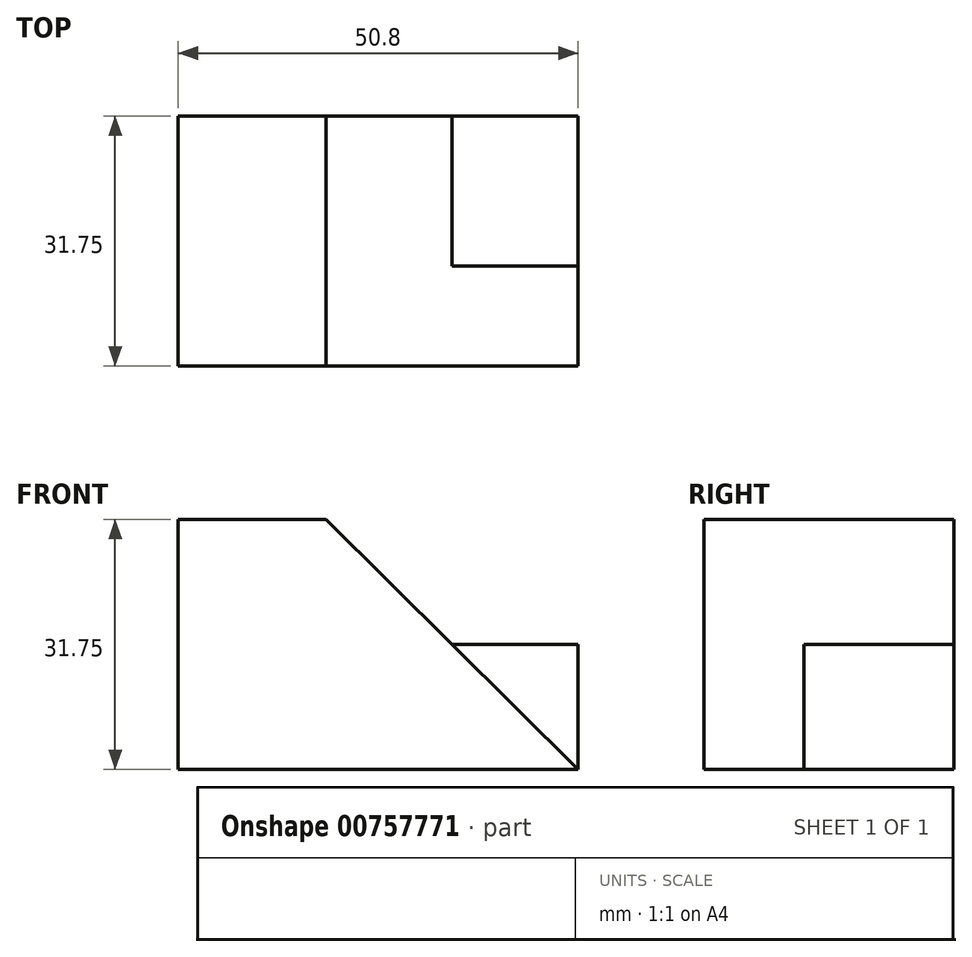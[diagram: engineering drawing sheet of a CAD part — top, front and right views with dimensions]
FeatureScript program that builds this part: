
annotation { "Feature Type Name" : "Feature", "Feature Type Description" : "" }
export const myFeature = defineFeature(function(context is Context, id is Id, definition is map)
    precondition{}
    {
        {
            var Q0;
            Q0=qCreatedBy(makeId("Front.planeOp"),FACE);
            var sketch = newSketch(context, id + "F0", { "sketchPlane" : qUnion([Q0])});
            skLineSegment(sketch, "E0", {"start": v(-18.76, 0) * mm, "end": v(32.04, 0) * mm});
            skLineSegment(sketch, "E1", {"start": v(32.04, 0) * mm, "end": v(32.04, 31.75) * mm});
            skLineSegment(sketch, "E2", {"start": v(32.04, 31.75) * mm, "end": v(-18.76, 31.75) * mm});
            skLineSegment(sketch, "E3", {"start": v(-18.76, 31.75) * mm, "end": v(-18.76, 0) * mm});
            skSolve(sketch);
        }
        {
            var Q0;
            Q0 = qSketchRegion(id + "F0", true);
            extrude(context, id + "F1", {"entities" : qUnion([Q0]), "depth" : 31.75 * mm, "offsetDistance" : 25.4 * mm});
        }
        {
            var Q0;
            Q0=makeQuery(id+"F1.opExtrude","CAP_FACE",FACE,{"disambiguationData":[OSD([sQuery(id+"F0.wireOp",EDGE,"E0"),sQuery(id+"F0.wireOp",EDGE,"E1"),sQuery(id+"F0.wireOp",EDGE,"E2"),sQuery(id+"F0.wireOp",EDGE,"E3")])],"isStart":false});
            var sketch = newSketch(context, id + "F2", { "sketchPlane" : qUnion([Q0])});
            skLineSegment(sketch, "E4", {"start": v(32.04, 0) * mm, "end": v(0, 31.75) * mm});
            skSolve(sketch);
        }
        {
            var Q0;
            {var subQ0=sQuery(id+"F2.wireOp",EDGE,"E4");Q0=makeQuery(id+"F2.imprint","IMPRINT",FACE,{"disambiguationData":[TD([[makeQuery(id+"F2.imprint","IMPRINT",EDGE,{"derivedFrom":subQ0}),-1.0]])]});}
            extrude(context, id + "F3", {"entities" : qUnion([Q0]), "operationType" : NewBodyOperationType.REMOVE, "oppositeDirection" : true, "depth" : 12.7 * mm, "offsetDistance" : 25.4 * mm});
        }
        {
            var Q0;
            Q0=makeQuery(id+"F3.boolean.opBoolean","COPY",FACE,{"derivedFrom":makeQuery(id+"F3.opExtrude","CAP_FACE",FACE,{"disambiguationData":[OSD([sQuery(id+"F0.wireOp",EDGE,"E1"),sQuery(id+"F0.wireOp",EDGE,"E2"),sQuery(id+"F2.wireOp",EDGE,"E4")])],"isStart":false})});
            var sketch = newSketch(context, id + "F4", { "sketchPlane" : qUnion([Q0])});
            skLineSegment(sketch, "E5", {"start": v(32.04, 0) * mm, "end": v(32.04, 15.88) * mm});
            skLineSegment(sketch, "E6", {"start": v(32.04, 15.88) * mm, "end": v(16.02, 15.87) * mm});
            skSolve(sketch);
        }
        {
            var Q0;
            Q0 = qSketchRegion(id + "F4", true);
            var Q1;
            {var subQ0=sQuery(id+"F4.wireOp",EDGE,"E6");Q1=makeQuery(id+"F4.imprint","IMPRINT",FACE,{"disambiguationData":[TD([[makeQuery(id+"F4.imprint","IMPRINT",EDGE,{"derivedFrom":subQ0}),-1.0]])]});}
            extrude(context, id + "F5", {"entities" : qUnion([Q0, Q1]), "operationType" : NewBodyOperationType.REMOVE, "endBound" : BoundingType.THROUGH_ALL, "oppositeDirection" : true, "depth" : 25.4 * mm, "offsetDistance" : 25.4 * mm});
        }
    });
